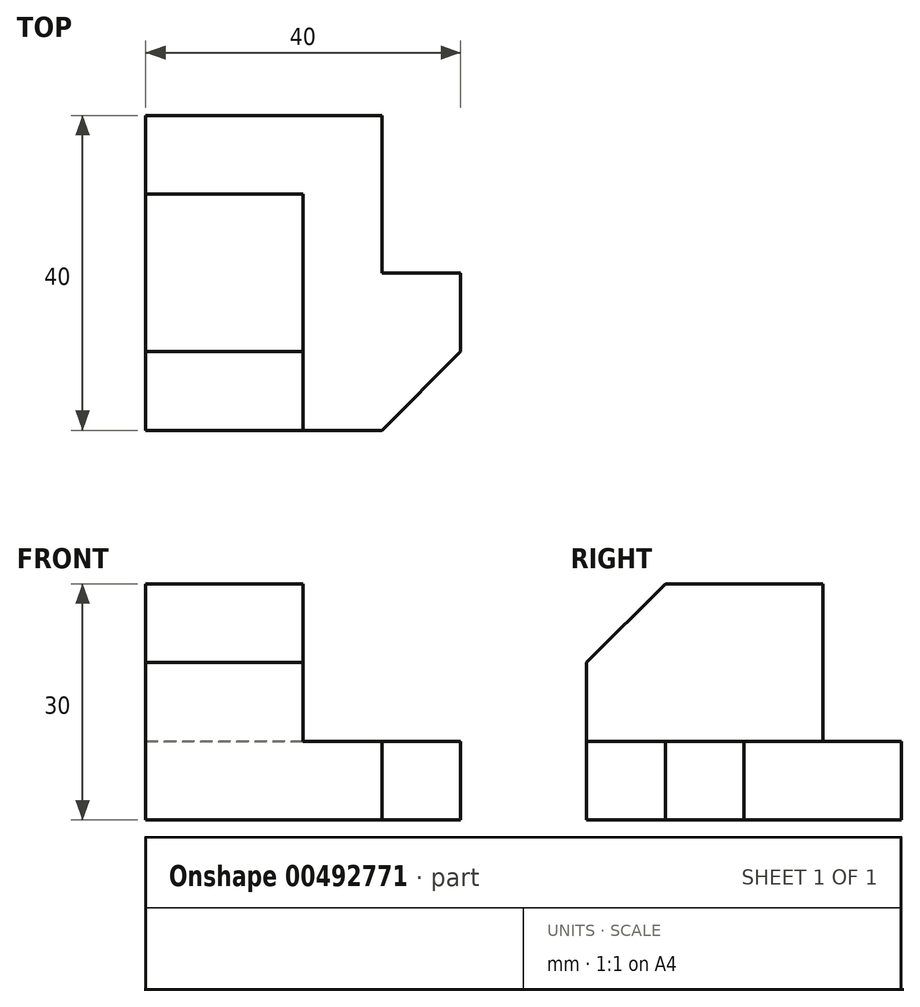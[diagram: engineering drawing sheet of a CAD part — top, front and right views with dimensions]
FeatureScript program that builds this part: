
annotation { "Feature Type Name" : "Feature", "Feature Type Description" : "" }
export const myFeature = defineFeature(function(context is Context, id is Id, definition is map)
    precondition{}
    {
        {
            var Q0;
            Q0=qCreatedBy(makeId("Top.planeOp"),FACE);
            var sketch = newSketch(context, id + "F0", { "sketchPlane" : qUnion([Q0])});
            skLineSegment(sketch, "E0", {"start": v(0, 0) * mm, "end": v(0, 40) * mm});
            skLineSegment(sketch, "E1", {"start": v(0, 40) * mm, "end": v(30, 40) * mm});
            skLineSegment(sketch, "E2", {"start": v(30, 40) * mm, "end": v(30, 20) * mm});
            skLineSegment(sketch, "E3", {"start": v(30, 20) * mm, "end": v(40, 20) * mm});
            skLineSegment(sketch, "E4", {"start": v(40, 20) * mm, "end": v(40, 10) * mm});
            skLineSegment(sketch, "E5", {"start": v(40, 10) * mm, "end": v(30, 0) * mm});
            skLineSegment(sketch, "E6", {"start": v(30, 0) * mm, "end": v(0, 0) * mm});
            skSolve(sketch);
        }
        {
            var Q0;
            Q0=makeQuery(id+"F0.imprint","IMPRINT",FACE,{"disambiguationData":[TD([[makeQuery(id+"F0.imprint","IMPRINT",EDGE,{"derivedFrom":sQuery(id+"F0.wireOp",EDGE,"E0")}),-1.0]])]});
            extrude(context, id + "F1", {"entities" : qUnion([Q0]), "depth" : 10 * mm});
        }
        {
            var Q0;
            Q0=makeQuery(id+"F1.opExtrude","CAP_FACE",FACE,{"disambiguationData":[OSD([sQuery(id+"F0.wireOp",EDGE,"E0"),sQuery(id+"F0.wireOp",EDGE,"E1"),sQuery(id+"F0.wireOp",EDGE,"E2"),sQuery(id+"F0.wireOp",EDGE,"E3"),sQuery(id+"F0.wireOp",EDGE,"E4"),sQuery(id+"F0.wireOp",EDGE,"E5"),sQuery(id+"F0.wireOp",EDGE,"E6")])],"isStart":false});
            var sketch = newSketch(context, id + "F2", { "sketchPlane" : qUnion([Q0])});
            skLineSegment(sketch, "E7", {"start": v(0, 0) * mm, "end": v(20, 0) * mm});
            skLineSegment(sketch, "E8", {"start": v(20, 0) * mm, "end": v(20, 30) * mm});
            skLineSegment(sketch, "E9", {"start": v(20, 30) * mm, "end": v(0, 30) * mm});
            skLineSegment(sketch, "E10", {"start": v(0, 30) * mm, "end": v(0, 0) * mm});
            skSolve(sketch);
        }
        {
            var Q0;
            Q0=makeQuery(id+"F2.imprint","IMPRINT",FACE,{"disambiguationData":[TD([[makeQuery(id+"F2.imprint","IMPRINT",EDGE,{"derivedFrom":sQuery(id+"F2.wireOp",EDGE,"E7")}),-1.0]])]});
            extrude(context, id + "F3", {"entities" : qUnion([Q0]), "operationType" : NewBodyOperationType.ADD, "depth" : 20 * mm});
        }
        {
            var Q0;
            Q0=makeQuery(id+"F3.opExtrude","CAP_EDGE",EDGE,{"disambiguationData":[OSD([sQuery(id+"F2.wireOp",EDGE,"E7")])],"isStart":false});
            chamfer(context, id + "F4", {"entities" : qUnion([Q0]), "width" : 10 * mm, "tangentPropagation" : true});
        }
    });
